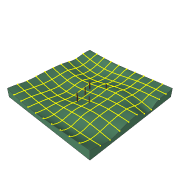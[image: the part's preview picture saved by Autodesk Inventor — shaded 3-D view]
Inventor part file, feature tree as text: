
AUTODESK INVENTOR PART (.ipt)
format: ipt  version: 2021 (Build 250183000, 183)  size: 2,512,896 bytes
history: native  units: in
note: dims shown in document units (in); Inventor stores cm internally (conversion verified against a paired STEP export)
features: sketch x12, projected_geometry x11, extrude x6, plane x3, fillet x1, loft x1, other x1
ambient origin geometry x8: Origin, YZ Plane, XZ Plane, XY Plane, X Axis, Y Axis, Z Axis, Center Point
bodies: Solid1 (feature_tree)
feature tree (35):
  extrude  "Extrusion1"  Depth=3937.0079in
  extrude  "Extrusion2"  Depth=157.4803in
  fillet  "Fillet1"  Radius=393.7008in
  extrude  "Extrusion3"  Depth=118.1102in TaperAngle=0.0deg
  extrude  "Extrusion4"  [1 undecoded]
  sketch  "Sketch5"  dims[d25=-3052.3125in d26=0.0in d27=90.0deg]
  sketch  "Sketch6"  dims[d28=0.0in d29=90.0deg d30=0.0in d31=90.0deg]
  plane  "Work Plane1"
  sketch  "Sketch7"  dims[d32=0.0in d33=90.0deg d34=590.5512in d35=0.0in]
  plane  "Work Plane2"
  loft  "Loft3"
  extrude  "Extrusion6"  TaperAngle=0.0deg  [1 undecoded]
  extrude  "Extrusion7"  Depth=590.5512in TaperAngle=0.0deg
  plane  "Work Plane3"
  sketch  "Sketch11"  dims[d40=3.5433in d42=393.7008in d43=0.3937in d45=1.0in d47=393.7008in d48=3.5433in d50=393.7008in d51=0.3937in d53=1.0in]
  sketch  "3D Sketch2"
  sketch  "Sketch1"  dims[d0=3937.0079in d1=3937.0079in]
  sketch  "Sketch2"  dims[d2=393.7008in d3=0.0in d4=157.4803in d5=393.7008in d6=0.0in]
  projected_geometry  "Projected Loop1"
  sketch  "Sketch3"  dims[d7=19.685in d8=118.1102in d9=0.0in]
  projected_geometry  "Projected Loop2"
  sketch  "Sketch4"  dims[d10=1.0in d11=0.0in d18=-808.3125in]
  projected_geometry  "Projected Loop3"
  projected_geometry  "Projected Loop4"
  projected_geometry  "Projected Loop5"
  projected_geometry  "Projected Loop6"
  sketch  "Sketch8"  dims[d36=196.8504in d37=0.0in]
  sketch  "Sketch9"  dims[d38=-1689.875in]
  sketch  "Sketch10"  dims[d39=393.7008in]
  projected_geometry  "Projected Loop7"
  projected_geometry  "Projected Loop8"
  projected_geometry  "Projected Loop9"
  projected_geometry  "Projected Loop10"
  projected_geometry  "Projected Loop11"
  other  "Project to Surface2"
note: 2 required parameter values undecoded (feature->parameter linkage not recoverable at this tier; creation-order binding heuristic only, values carry confidence <= 0.55)
